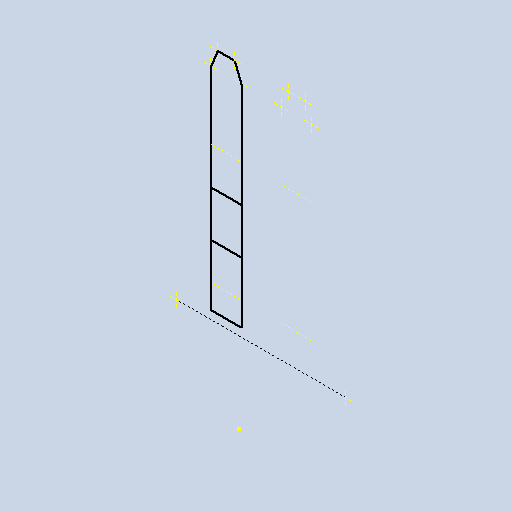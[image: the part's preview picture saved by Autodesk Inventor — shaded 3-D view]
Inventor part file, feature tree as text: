
AUTODESK INVENTOR PART (.ipt)
format: ipt  version: 2022.1 (Build 261234000, 234)  size: 77,312 bytes
history: native  units: mm
features: reference x14, other x2, sketch x1
ambient origin geometry x8: Origin, YZ Plane, XZ Plane, XY Plane, X Axis, Y Axis, Z Axis, Center Point
feature tree (17):
  sketch  "Sketch1"  dims[d2=50.0mm d4=220.0mm d6=220.0mm]
  reference  "Reference1"
  reference  "Reference2"
  reference  "Reference3"
  reference  "Reference4"
  reference  "Reference5"
  reference  "Reference6"
  reference  "Reference7"
  reference  "Reference8"
  reference  "Reference9"
  reference  "Reference10"
  reference  "Reference13"
  reference  "Reference14"
  reference  "Reference15"
  reference  "Reference16"
  other  "EstructuraInferior - Soldadura.iam"
  other  "EstructuraInferior_Esqueleto:1"
